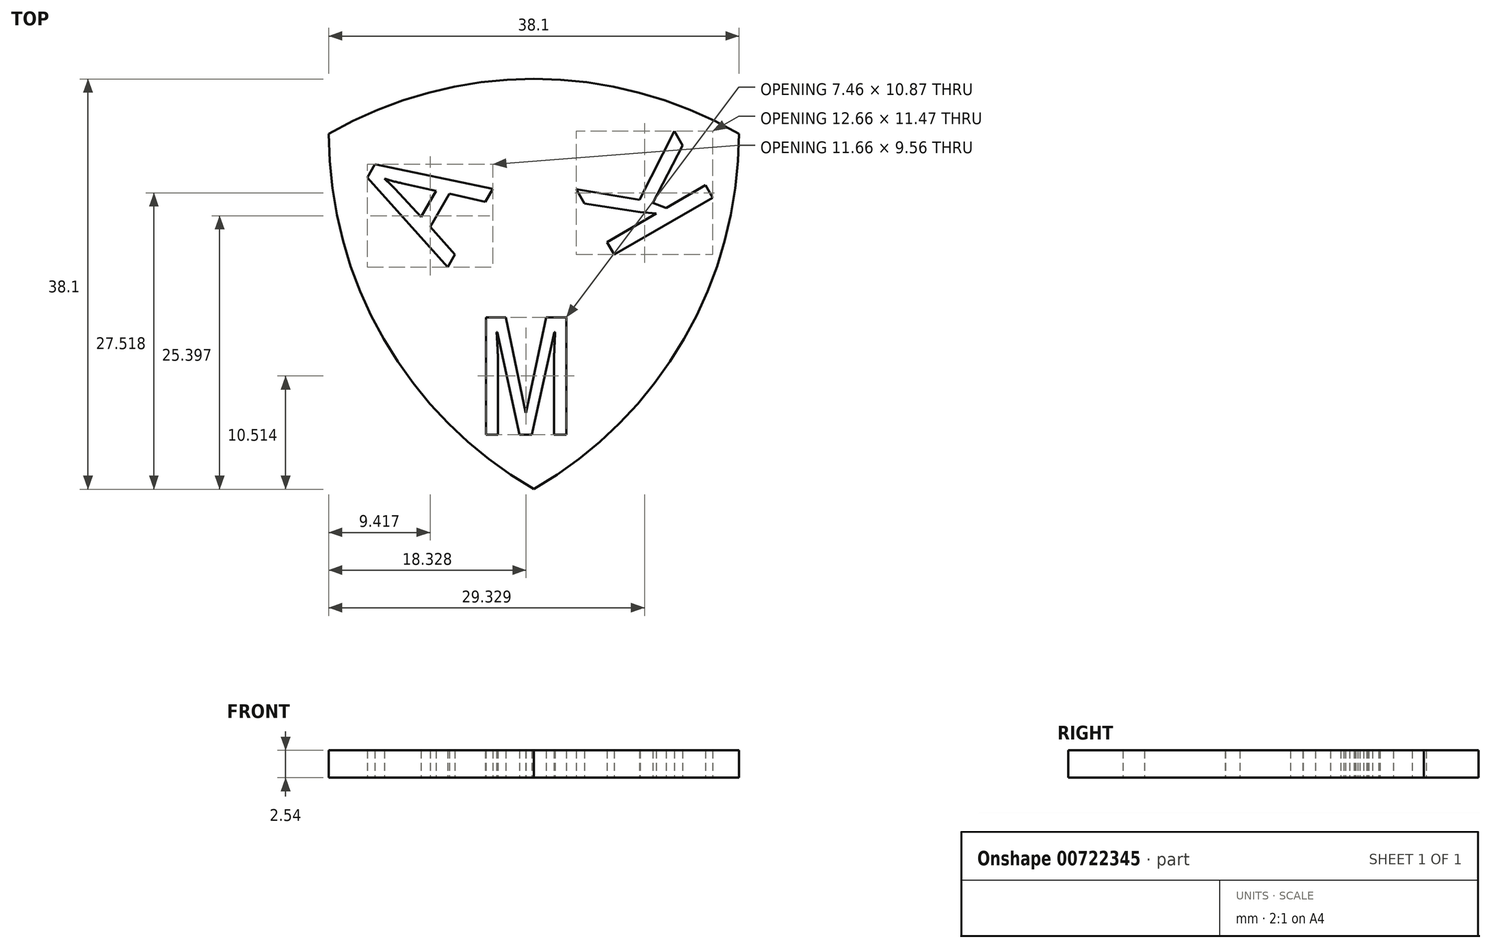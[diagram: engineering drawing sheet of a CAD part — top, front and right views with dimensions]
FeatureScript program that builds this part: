
annotation { "Feature Type Name" : "Feature", "Feature Type Description" : "" }
export const myFeature = defineFeature(function(context is Context, id is Id, definition is map)
    precondition{}
    {
        {
            var Q0;
            Q0=qCreatedBy(makeId("Top.planeOp"),FACE);
            var sketch = newSketch(context, id + "F0", { "sketchPlane" : qUnion([Q0])});
            skCircle(sketch, "E0", {"center": v(0, 0) * mm, "radius": 38.1 * mm});
            skSolve(sketch);
        }
        {
            var Q0;
            Q0=qCreatedBy(makeId("Top.planeOp"),FACE);
            var sketch = newSketch(context, id + "F1", { "sketchPlane" : qUnion([Q0])});
            skCircle(sketch, "E1", {"center": v(-38.1, 0) * mm, "radius": 38.1 * mm});
            skSolve(sketch);
        }
        {
            var Q0;
            Q0=qCreatedBy(makeId("Top.planeOp"),FACE);
            var sketch = newSketch(context, id + "F2", { "sketchPlane" : qUnion([Q0])});
            skCircle(sketch, "E2", {"center": v(-19.05, -33) * mm, "radius": 38.1 * mm});
            skSolve(sketch);
        }
        {
            var Q0;
            Q0 = qSketchRegion(id + "F0", true);
            extrude(context, id + "F3", {"entities" : qUnion([Q0]), "depth" : 2.54 * mm, "offsetDistance" : 25.4 * mm});
        }
        {
            var Q0;
            Q0 = qSketchRegion(id + "F1", true);
            extrude(context, id + "F4", {"entities" : qUnion([Q0]), "depth" : 2.54 * mm, "offsetDistance" : 25.4 * mm});
        }
        {
            var Q0;
            Q0 = qSketchRegion(id + "F2", true);
            extrude(context, id + "F5", {"entities" : qUnion([Q0]), "depth" : 2.54 * mm, "offsetDistance" : 25.4 * mm});
        }
        {
            var Q0;
            Q0=makeQuery(id+"F4.opExtrude","SWEPT_BODY",BODY,{"disambiguationData":[OSD([sQuery(id+"F1.wireOp",EDGE,"E1")])]});
            var Q1;
            Q1=makeQuery(id+"F3.opExtrude","SWEPT_BODY",BODY,{"disambiguationData":[OSD([sQuery(id+"F0.wireOp",EDGE,"E0")])]});
            var Q2;
            Q2=makeQuery(id+"F5.opExtrude","SWEPT_BODY",BODY,{"disambiguationData":[OSD([sQuery(id+"F2.wireOp",EDGE,"E2")])]});
            booleanBodies(context, id + "F6", {"operationType" : BooleanOperationType.INTERSECTION, "tools" : qUnion([Q0, Q1, Q2])});
        }
        {
            var Q0;
            Q0=qCreatedBy(makeId("Top.planeOp"),FACE);
            var sketch = newSketch(context, id + "F7", { "sketchPlane" : qUnion([Q0])});
            skText(sketch, "E3", { "text": "A", "fontName": "DroidSansMono.ttf"});
            skText(sketch, "E4", { "text": "M", "fontName": "DroidSansMono.ttf"});
            skText(sketch, "E5", { "text": "K", "fontName": "DroidSansMono.ttf"});
            const initialGuessF7  = {"E3": [-0.02718, -0.01259, 0.5, 0.86603, 0.01067], "E4": [-0.02434, -0.02792, 1, 0, 0.01096], "E5": [-0.00168, -0.00725, -0.5, 0.86603, 0.01066]};
            skSetInitialGuess(sketch, initialGuessF7);
            skSolve(sketch);
        }
        {
            var Q0;
            Q0 = qSketchRegion(id + "F7", true);
            extrude(context, id + "F8", {"entities" : qUnion([Q0]), "depth" : 2.54 * mm, "offsetDistance" : 25.4 * mm});
        }
        {
            var Q0;
            Q0=makeQuery(id+"F8.opExtrude","SWEPT_BODY",BODY,{"disambiguationData":[OSD([sQuery(id+"F7.wireOp",EDGE,"E3.sketch_text.stroke-0"),sQuery(id+"F7.wireOp",EDGE,"E3.sketch_text.stroke-1"),sQuery(id+"F7.wireOp",EDGE,"E3.sketch_text.stroke-2"),sQuery(id+"F7.wireOp",EDGE,"E3.sketch_text.stroke-3"),sQuery(id+"F7.wireOp",EDGE,"E3.sketch_text.stroke-4"),sQuery(id+"F7.wireOp",EDGE,"E3.sketch_text.stroke-5"),sQuery(id+"F7.wireOp",EDGE,"E3.sketch_text.stroke-6"),sQuery(id+"F7.wireOp",EDGE,"E3.sketch_text.stroke-7"),sQuery(id+"F7.wireOp",EDGE,"E3.sketch_text.stroke-8"),sQuery(id+"F7.wireOp",EDGE,"E3.sketch_text.stroke-9"),sQuery(id+"F7.wireOp",EDGE,"E3.sketch_text.stroke-10"),sQuery(id+"F7.wireOp",EDGE,"E3.sketch_text.stroke-11"),sQuery(id+"F7.wireOp",EDGE,"E3.sketch_text.stroke-12")])]});
            var Q1;
            Q1=makeQuery(id+"F8.opExtrude","SWEPT_BODY",BODY,{"disambiguationData":[OSD([sQuery(id+"F7.wireOp",EDGE,"E5.sketch_text.stroke-0"),sQuery(id+"F7.wireOp",EDGE,"E5.sketch_text.stroke-1"),sQuery(id+"F7.wireOp",EDGE,"E5.sketch_text.stroke-2"),sQuery(id+"F7.wireOp",EDGE,"E5.sketch_text.stroke-3"),sQuery(id+"F7.wireOp",EDGE,"E5.sketch_text.stroke-4"),sQuery(id+"F7.wireOp",EDGE,"E5.sketch_text.stroke-5"),sQuery(id+"F7.wireOp",EDGE,"E5.sketch_text.stroke-6"),sQuery(id+"F7.wireOp",EDGE,"E5.sketch_text.stroke-7"),sQuery(id+"F7.wireOp",EDGE,"E5.sketch_text.stroke-8"),sQuery(id+"F7.wireOp",EDGE,"E5.sketch_text.stroke-9"),sQuery(id+"F7.wireOp",EDGE,"E5.sketch_text.stroke-10"),sQuery(id+"F7.wireOp",EDGE,"E5.sketch_text.stroke-11"),sQuery(id+"F7.wireOp",EDGE,"E5.sketch_text.stroke-12")])]});
            var Q2;
            Q2=makeQuery(id+"F8.opExtrude","SWEPT_BODY",BODY,{"disambiguationData":[OSD([sQuery(id+"F7.wireOp",EDGE,"E4.sketch_text.stroke-0"),sQuery(id+"F7.wireOp",EDGE,"E4.sketch_text.stroke-1"),sQuery(id+"F7.wireOp",EDGE,"E4.sketch_text.stroke-2"),sQuery(id+"F7.wireOp",EDGE,"E4.sketch_text.stroke-3"),sQuery(id+"F7.wireOp",EDGE,"E4.sketch_text.stroke-4"),sQuery(id+"F7.wireOp",EDGE,"E4.sketch_text.stroke-5"),sQuery(id+"F7.wireOp",EDGE,"E4.sketch_text.stroke-6"),sQuery(id+"F7.wireOp",EDGE,"E4.sketch_text.stroke-7"),sQuery(id+"F7.wireOp",EDGE,"E4.sketch_text.stroke-8"),sQuery(id+"F7.wireOp",EDGE,"E4.sketch_text.stroke-9"),sQuery(id+"F7.wireOp",EDGE,"E4.sketch_text.stroke-10"),sQuery(id+"F7.wireOp",EDGE,"E4.sketch_text.stroke-11"),sQuery(id+"F7.wireOp",EDGE,"E4.sketch_text.stroke-12"),sQuery(id+"F7.wireOp",EDGE,"E4.sketch_text.stroke-13"),sQuery(id+"F7.wireOp",EDGE,"E4.sketch_text.stroke-14"),sQuery(id+"F7.wireOp",EDGE,"E4.sketch_text.stroke-15"),sQuery(id+"F7.wireOp",EDGE,"E4.sketch_text.stroke-16"),sQuery(id+"F7.wireOp",EDGE,"E4.sketch_text.stroke-17")])]});
            var Q3;
            Q3=makeQuery(id+"F6.opBoolean","INTERSECT",BODY,{"derivedFrom":[makeQuery(id+"F3.opExtrude","SWEPT_BODY",BODY,{"disambiguationData":[OSD([sQuery(id+"F0.wireOp",EDGE,"E0")])]}),makeQuery(id+"F4.opExtrude","SWEPT_BODY",BODY,{"disambiguationData":[OSD([sQuery(id+"F1.wireOp",EDGE,"E1")])]}),makeQuery(id+"F5.opExtrude","SWEPT_BODY",BODY,{"disambiguationData":[OSD([sQuery(id+"F2.wireOp",EDGE,"E2")])]})]});
            booleanBodies(context, id + "F9", {"operationType" : BooleanOperationType.SUBTRACTION, "tools" : qUnion([Q0, Q1, Q2]), "targets" : qUnion([Q3])});
        }
    });
